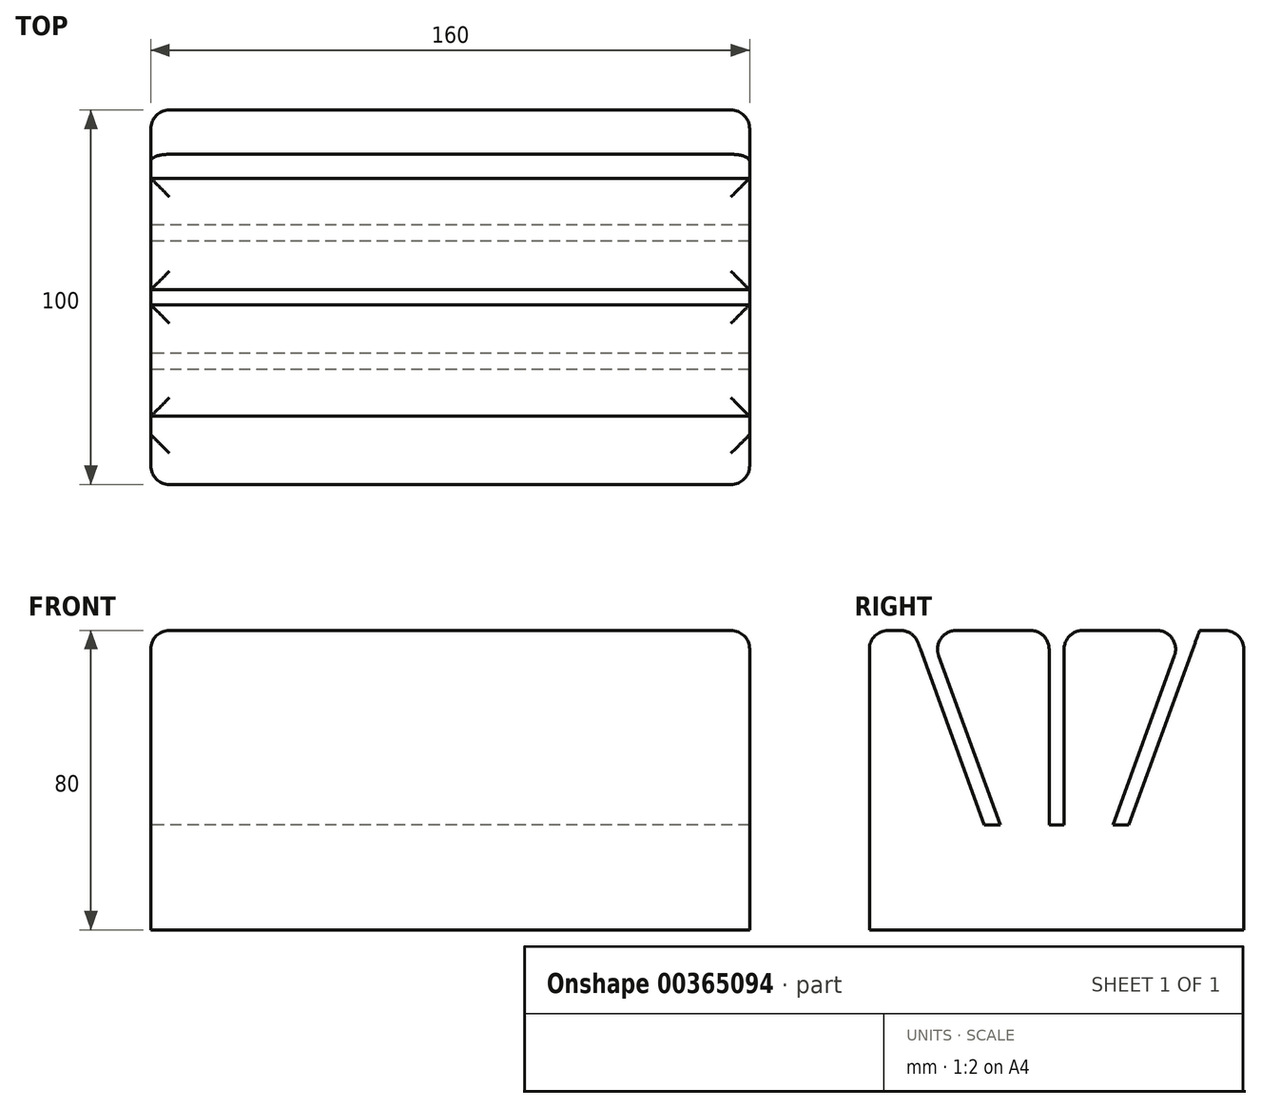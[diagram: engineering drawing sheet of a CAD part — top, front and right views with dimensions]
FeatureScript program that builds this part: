
annotation { "Feature Type Name" : "Feature", "Feature Type Description" : "" }
export const myFeature = defineFeature(function(context is Context, id is Id, definition is map)
    precondition{}
    {
        {
            var Q0;
            Q0=qCreatedBy(makeId("Top.planeOp"),FACE);
            var sketch = newSketch(context, id + "F0", { "sketchPlane" : qUnion([Q0])});
            skLineSegment(sketch, "E0.bottom", {"start": v(0, 0) * mm, "end": v(160, 0) * mm});
            skLineSegment(sketch, "E0.top", {"start": v(0, 100) * mm, "end": v(160, 100) * mm});
            skLineSegment(sketch, "E0.left", {"start": v(0, 0) * mm, "end": v(0, 100) * mm});
            skLineSegment(sketch, "E0.right", {"start": v(160, 0) * mm, "end": v(160, 100) * mm});
            skSolve(sketch);
        }
        {
            var Q0;
            Q0=makeQuery(id+"F0.imprint","IMPRINT",FACE,{"disambiguationData":[TD([[makeQuery(id+"F0.imprint","IMPRINT",EDGE,{"derivedFrom":sQuery(id+"F0.wireOp",EDGE,"E0.bottom")}),1.0]])]});
            extrude(context, id + "F1", {"entities" : qUnion([Q0]), "depth" : 80 * mm});
        }
        {
            var Q0;
            Q0=makeQuery(id+"F1.opExtrude","SWEPT_FACE",FACE,{"disambiguationData":[OSD([sQuery(id+"F0.wireOp",EDGE,"E0.left")])]});
            var sketch = newSketch(context, id + "F2", { "sketchPlane" : qUnion([Q0])});
            skLineSegment(sketch, "E1", {"start": v(-11.8, 80) * mm, "end": v(-30.72, 28) * mm});
            skLineSegment(sketch, "E2", {"start": v(-34.98, 28) * mm, "end": v(-16.05, 80) * mm});
            skLineSegment(sketch, "E3", {"start": v(-16.05, 80) * mm, "end": v(-11.8, 80) * mm});
            skLineSegment(sketch, "E4.bottom", {"start": v(-48, 80) * mm, "end": v(-52, 80) * mm});
            skLineSegment(sketch, "E4.left", {"start": v(-48, 80) * mm, "end": v(-48, 28) * mm});
            skLineSegment(sketch, "E4.right", {"start": v(-52, 80) * mm, "end": v(-52, 28) * mm});
            skLineSegment(sketch, "E5", {"start": v(-30.72, 28) * mm, "end": v(-34.98, 28) * mm});
            skPoint(sketch, "E6.orphan", {"position": v(-45.17, 0) * mm});
            skLineSegment(sketch, "E7", {"start": v(-48, 28) * mm, "end": v(-52, 28) * mm});
            skLineSegment(sketch, "E8.0", {"start": v(-100, 80) * mm, "end": v(-100, 0) * mm});
            skLineSegment(sketch, "E9.0", {"start": v(0, 80) * mm, "end": v(0, 0) * mm});
            skLineSegment(sketch, "E10", {"start": v(-48, 80) * mm, "end": v(-50, 80) * mm, "construction": true});
            skLineSegment(sketch, "E11", {"start": v(-50, 80) * mm, "end": v(-50, 38.93) * mm, "construction": true});
            skLineSegment(sketch, "E12.MirrorCS", {"start": v(-65.02, 28) * mm, "end": v(-83.95, 80) * mm});
            skLineSegment(sketch, "E13.MirrorCS", {"start": v(-88.2, 80) * mm, "end": v(-69.28, 28) * mm});
            skLineSegment(sketch, "E14.MirrorCS", {"start": v(-69.28, 28) * mm, "end": v(-65.02, 28) * mm});
            skLineSegment(sketch, "E15.MirrorCS", {"start": v(-83.95, 80) * mm, "end": v(-88.2, 80) * mm});
            skSolve(sketch);
        }
        {
            var Q0;
            Q0=makeQuery(id+"F2.imprint","IMPRINT",FACE,{"disambiguationData":[TD([[makeQuery(id+"F2.imprint","IMPRINT",EDGE,{"derivedFrom":sQuery(id+"F2.wireOp",EDGE,"E12.MirrorCS")}),1.0]])]});
            var Q1;
            Q1=makeQuery(id+"F2.imprint","IMPRINT",FACE,{"disambiguationData":[TD([[makeQuery(id+"F2.imprint","IMPRINT",EDGE,{"derivedFrom":sQuery(id+"F2.wireOp",EDGE,"E4.bottom")}),1.0]])]});
            var Q2;
            Q2=makeQuery(id+"F2.imprint","IMPRINT",FACE,{"disambiguationData":[TD([[makeQuery(id+"F2.imprint","IMPRINT",EDGE,{"derivedFrom":sQuery(id+"F2.wireOp",EDGE,"E1")}),-1.0]])]});
            var Q3;
            Q3=makeQuery(id+"F1.opExtrude","SWEPT_FACE",FACE,{"disambiguationData":[OSD([sQuery(id+"F0.wireOp",EDGE,"E0.right")])]});
            extrude(context, id + "F3", {"entities" : qUnion([Q0, Q1, Q2]), "operationType" : NewBodyOperationType.REMOVE, "endBound" : BoundingType.UP_TO_SURFACE, "oppositeDirection" : true, "endBoundEntityFace" : qUnion([Q3]), "depth" : 25 * mm});
        }
        {
            var Q0;
            Q0=makeQuery(id+"F1.opExtrude","CAP_EDGE",EDGE,{"disambiguationData":[OSD([sQuery(id+"F0.wireOp",EDGE,"E0.bottom")])],"isStart":false});
            var Q1;
            Q1=makeQuery(id+"F1.opExtrude","CAP_EDGE",EDGE,{"disambiguationData":[OSD([sQuery(id+"F0.wireOp",EDGE,"E0.top")])],"isStart":false});
            var Q2;
            {var subQ0=sQuery(id+"F0.wireOp",EDGE,"E0.right");var subQ1=sQuery(id+"F0.wireOp",EDGE,"E0.top");Q2=makeQuery(id+"F3.boolean.opBoolean","SPLIT",EDGE,{"disambiguationData":[TD([makeQuery(id+"F1.opExtrude","SWEPT_FACE",FACE,{"disambiguationData":[OSD([subQ1])]})])],"derivedFrom":makeQuery(id+"F1.opExtrude","CAP_EDGE",EDGE,{"disambiguationData":[OSD([subQ0])],"isStart":false})});}
            var Q3;
            {var subQ0=sQuery(id+"F0.wireOp",EDGE,"E0.right");Q3=makeQuery(id+"F3.boolean.opBoolean","SPLIT",EDGE,{"disambiguationData":[TD([makeQuery(id+"F3.opExtrude","SWEPT_FACE",FACE,{"disambiguationData":[OSD([sQuery(id+"F2.wireOp",EDGE,"E4.right")])]})])],"derivedFrom":makeQuery(id+"F1.opExtrude","CAP_EDGE",EDGE,{"disambiguationData":[OSD([subQ0])],"isStart":false})});}
            var Q4;
            {var subQ0=sQuery(id+"F0.wireOp",EDGE,"E0.right");Q4=makeQuery(id+"F3.boolean.opBoolean","SPLIT",EDGE,{"disambiguationData":[TD([makeQuery(id+"F3.opExtrude","SWEPT_FACE",FACE,{"disambiguationData":[OSD([sQuery(id+"F2.wireOp",EDGE,"E2")])]})])],"derivedFrom":makeQuery(id+"F1.opExtrude","CAP_EDGE",EDGE,{"disambiguationData":[OSD([subQ0])],"isStart":false})});}
            var Q5;
            {var subQ0=sQuery(id+"F0.wireOp",EDGE,"E0.bottom");var subQ1=sQuery(id+"F0.wireOp",EDGE,"E0.right");Q5=makeQuery(id+"F3.boolean.opBoolean","SPLIT",EDGE,{"disambiguationData":[TD([makeQuery(id+"F1.opExtrude","SWEPT_FACE",FACE,{"disambiguationData":[OSD([subQ0])]})])],"derivedFrom":makeQuery(id+"F1.opExtrude","CAP_EDGE",EDGE,{"disambiguationData":[OSD([subQ1])],"isStart":false})});}
            var Q6;
            {var subQ0=sQuery(id+"F0.wireOp",EDGE,"E0.bottom");var subQ1=sQuery(id+"F0.wireOp",EDGE,"E0.left");Q6=makeQuery(id+"F3.boolean.opBoolean","SPLIT",EDGE,{"disambiguationData":[TD([makeQuery(id+"F1.opExtrude","SWEPT_FACE",FACE,{"disambiguationData":[OSD([subQ0])]})])],"derivedFrom":makeQuery(id+"F1.opExtrude","CAP_EDGE",EDGE,{"disambiguationData":[OSD([subQ1])],"isStart":false})});}
            var Q7;
            {var subQ0=sQuery(id+"F0.wireOp",EDGE,"E0.left");Q7=makeQuery(id+"F3.boolean.opBoolean","SPLIT",EDGE,{"disambiguationData":[TD([makeQuery(id+"F3.opExtrude","SWEPT_FACE",FACE,{"disambiguationData":[OSD([sQuery(id+"F2.wireOp",EDGE,"E2")])]})])],"derivedFrom":makeQuery(id+"F1.opExtrude","CAP_EDGE",EDGE,{"disambiguationData":[OSD([subQ0])],"isStart":false})});}
            var Q8;
            {var subQ0=sQuery(id+"F0.wireOp",EDGE,"E0.left");Q8=makeQuery(id+"F3.boolean.opBoolean","SPLIT",EDGE,{"disambiguationData":[TD([makeQuery(id+"F3.opExtrude","SWEPT_FACE",FACE,{"disambiguationData":[OSD([sQuery(id+"F2.wireOp",EDGE,"E4.right")])]})])],"derivedFrom":makeQuery(id+"F1.opExtrude","CAP_EDGE",EDGE,{"disambiguationData":[OSD([subQ0])],"isStart":false})});}
            var Q9;
            {var subQ0=sQuery(id+"F0.wireOp",EDGE,"E0.left");var subQ1=sQuery(id+"F0.wireOp",EDGE,"E0.top");Q9=makeQuery(id+"F3.boolean.opBoolean","SPLIT",EDGE,{"disambiguationData":[TD([makeQuery(id+"F1.opExtrude","SWEPT_FACE",FACE,{"disambiguationData":[OSD([subQ1])]})])],"derivedFrom":makeQuery(id+"F1.opExtrude","CAP_EDGE",EDGE,{"disambiguationData":[OSD([subQ0])],"isStart":false})});}
            var Q10;
            Q10=makeQuery(id+"F1.opExtrude","SWEPT_EDGE",EDGE,{"disambiguationData":[OSD([sQuery(id+"F0.wireOp",EDGE,"E0.top"),sQuery(id+"F0.wireOp",EDGE,"E0.right")])]});
            var Q11;
            Q11=makeQuery(id+"F1.opExtrude","SWEPT_EDGE",EDGE,{"disambiguationData":[OSD([sQuery(id+"F0.wireOp",EDGE,"E0.top"),sQuery(id+"F0.wireOp",EDGE,"E0.left")])]});
            var Q12;
            Q12=makeQuery(id+"F1.opExtrude","SWEPT_EDGE",EDGE,{"disambiguationData":[OSD([sQuery(id+"F0.wireOp",EDGE,"E0.bottom"),sQuery(id+"F0.wireOp",EDGE,"E0.right")])]});
            var Q13;
            Q13=makeQuery(id+"F1.opExtrude","SWEPT_EDGE",EDGE,{"disambiguationData":[OSD([sQuery(id+"F0.wireOp",EDGE,"E0.bottom"),sQuery(id+"F0.wireOp",EDGE,"E0.left")])]});
            var Q14;
            Q14=makeQuery(id+"F3.boolean.opBoolean","COPY",EDGE,{"derivedFrom":makeQuery(id+"F3.opExtrude","SWEPT_EDGE",EDGE,{"disambiguationData":[OSD([sQuery(id+"F0.wireOp",EDGE,"E0.left"),sQuery(id+"F2.wireOp",EDGE,"E4.bottom"),sQuery(id+"F2.wireOp",EDGE,"E4.left")])]})});
            var Q15;
            Q15=makeQuery(id+"F3.boolean.opBoolean","COPY",EDGE,{"derivedFrom":makeQuery(id+"F3.opExtrude","SWEPT_EDGE",EDGE,{"disambiguationData":[OSD([sQuery(id+"F0.wireOp",EDGE,"E0.left"),sQuery(id+"F2.wireOp",EDGE,"E4.bottom"),sQuery(id+"F2.wireOp",EDGE,"E4.right")])]})});
            var Q16;
            Q16=makeQuery(id+"F3.boolean.opBoolean","COPY",EDGE,{"derivedFrom":makeQuery(id+"F3.opExtrude","SWEPT_EDGE",EDGE,{"disambiguationData":[OSD([sQuery(id+"F0.wireOp",EDGE,"E0.left"),sQuery(id+"F2.wireOp",EDGE,"E12.MirrorCS"),sQuery(id+"F2.wireOp",EDGE,"E15.MirrorCS")])]})});
            var Q17;
            Q17=makeQuery(id+"F3.boolean.opBoolean","COPY",EDGE,{"derivedFrom":makeQuery(id+"F3.opExtrude","SWEPT_EDGE",EDGE,{"disambiguationData":[OSD([sQuery(id+"F0.wireOp",EDGE,"E0.left"),sQuery(id+"F2.wireOp",EDGE,"E13.MirrorCS"),sQuery(id+"F2.wireOp",EDGE,"E15.MirrorCS")])]})});
            var Q18;
            Q18=makeQuery(id+"F3.boolean.opBoolean","COPY",EDGE,{"derivedFrom":makeQuery(id+"F3.opExtrude","SWEPT_EDGE",EDGE,{"disambiguationData":[OSD([sQuery(id+"F0.wireOp",EDGE,"E0.left"),sQuery(id+"F2.wireOp",EDGE,"E2"),sQuery(id+"F2.wireOp",EDGE,"E3")])]})});
            var Q19;
            Q19=makeQuery(id+"F3.boolean.opBoolean","COPY",EDGE,{"derivedFrom":makeQuery(id+"F3.opExtrude","SWEPT_EDGE",EDGE,{"disambiguationData":[OSD([sQuery(id+"F0.wireOp",EDGE,"E0.left"),sQuery(id+"F2.wireOp",EDGE,"E1"),sQuery(id+"F2.wireOp",EDGE,"E3")])]})});
            fillet(context, id + "F4", {"entities" : qUnion([Q0, Q1, Q2, Q3, Q4, Q5, Q6, Q7, Q8, Q9, Q10, Q11, Q12, Q13, Q14, Q15, Q16, Q17, Q18, Q19]), "radius" : 5 * mm, "tangentPropagation" : true, "allowEdgeOverflow" : false});
        }
    });
